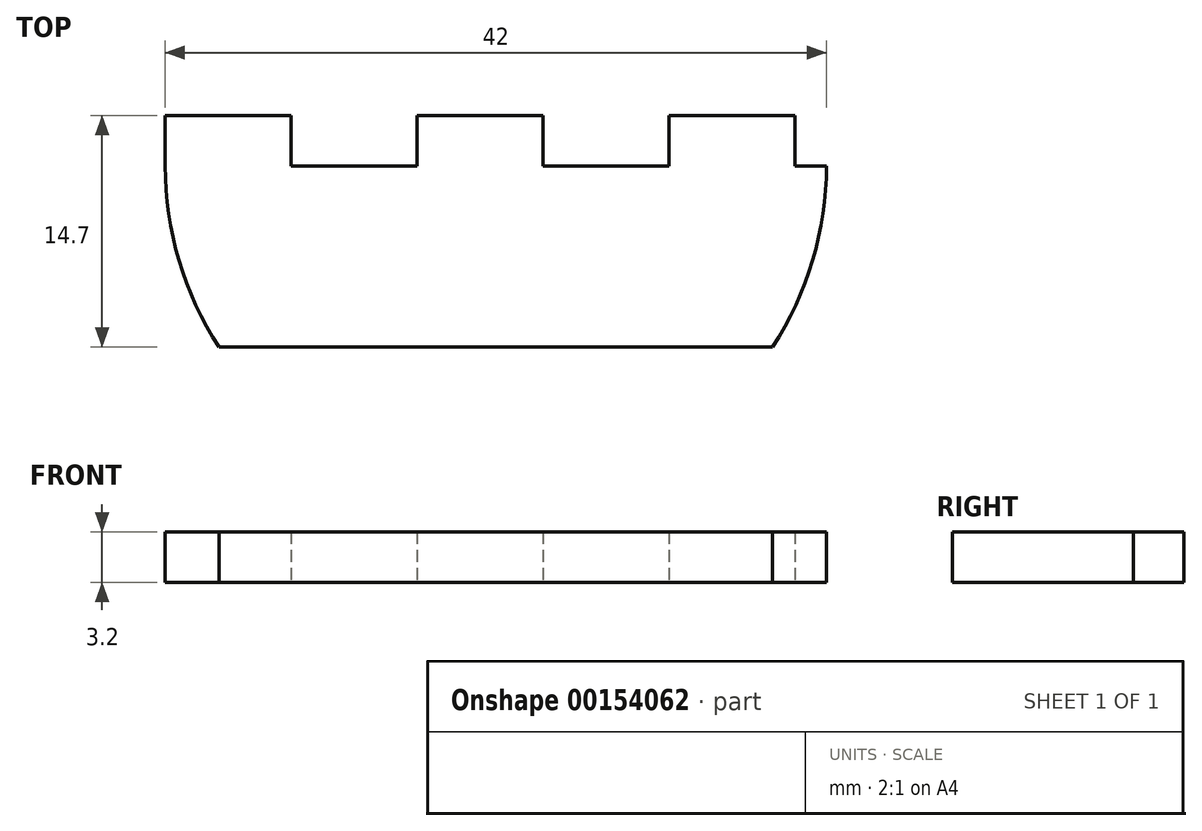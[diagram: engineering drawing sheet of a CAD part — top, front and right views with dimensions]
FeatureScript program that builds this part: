
annotation { "Feature Type Name" : "Feature", "Feature Type Description" : "" }
export const myFeature = defineFeature(function(context is Context, id is Id, definition is map)
    precondition{}
    {
        {
            var Q0;
            Q0=qCreatedBy(makeId("Top.planeOp"),FACE);
            var sketch = newSketch(context, id + "F0", { "sketchPlane" : qUnion([Q0])});
            skArc(sketch, "E0", {"start": v(-21, 0) * mm, "mid": v(-20.12, -6) * mm, "end": v(-17.57, -11.5) * mm});
            skLineSegment(sketch, "E1", {"start": v(-21, 0) * mm, "end": v(-21, 3.2) * mm});
            skLineSegment(sketch, "E2", {"start": v(-21, 3.2) * mm, "end": v(-13, 3.2) * mm});
            skLineSegment(sketch, "E3", {"start": v(-13, 3.2) * mm, "end": v(-13, 0) * mm});
            skLineSegment(sketch, "E4", {"start": v(-13, 0) * mm, "end": v(-5, 0) * mm});
            skLineSegment(sketch, "E5", {"start": v(-5, 0) * mm, "end": v(-5, 3.2) * mm});
            skLineSegment(sketch, "E6", {"start": v(-5, 3.2) * mm, "end": v(3, 3.2) * mm});
            skLineSegment(sketch, "E7", {"start": v(3, 3.2) * mm, "end": v(3, 0) * mm});
            skLineSegment(sketch, "E8", {"start": v(3, 0) * mm, "end": v(11, 0) * mm});
            skLineSegment(sketch, "E9", {"start": v(11, 0) * mm, "end": v(11, 3.2) * mm});
            skLineSegment(sketch, "E10", {"start": v(11, 3.2) * mm, "end": v(19, 3.2) * mm});
            skLineSegment(sketch, "E11", {"start": v(19, 3.2) * mm, "end": v(19, 0) * mm});
            skLineSegment(sketch, "E12", {"start": v(19, 0) * mm, "end": v(21, 0) * mm});
            skLineSegment(sketch, "E13", {"start": v(0, 0) * mm, "end": v(0, -21) * mm, "construction": true});
            skLineSegment(sketch, "E14", {"start": v(0, -21) * mm, "end": v(0, -11.5) * mm, "construction": true});
            skLineSegment(sketch, "E15", {"start": v(0, -11.5) * mm, "end": v(-17.57, -11.5) * mm});
            skLineSegment(sketch, "E16", {"start": v(-17.57, -11.5) * mm, "end": v(17.57, -11.5) * mm});
            skArc(sketch, "E17.trimOffspring", {"start": v(17.57, -11.5) * mm, "mid": v(20.12, -6) * mm, "end": v(21, 0) * mm});
            skSolve(sketch);
        }
        {
            var Q0;
            Q0=makeQuery(id+"F0.imprint","IMPRINT",FACE,{"disambiguationData":[TD([[makeQuery(id+"F0.imprint","IMPRINT",EDGE,{"derivedFrom":sQuery(id+"F0.wireOp",EDGE,"WeAqzrae-46Nc-yjBp-5vXX-3ru7yos8T8HK")}),1.0]])]});
            var Q1;
            Q1=makeQuery(id+"F0.imprint","IMPRINT",FACE,{"disambiguationData":[TD([[makeQuery(id+"F0.imprint","IMPRINT",EDGE,{"derivedFrom":sQuery(id+"F0.wireOp",EDGE,"E0")}),1.0]])]});
            extrude(context, id + "F1", {"entities" : qUnion([Q0, Q1]), "endBound" : BoundingType.SYMMETRIC, "depth" : 3.2 * mm});
        }
    });
